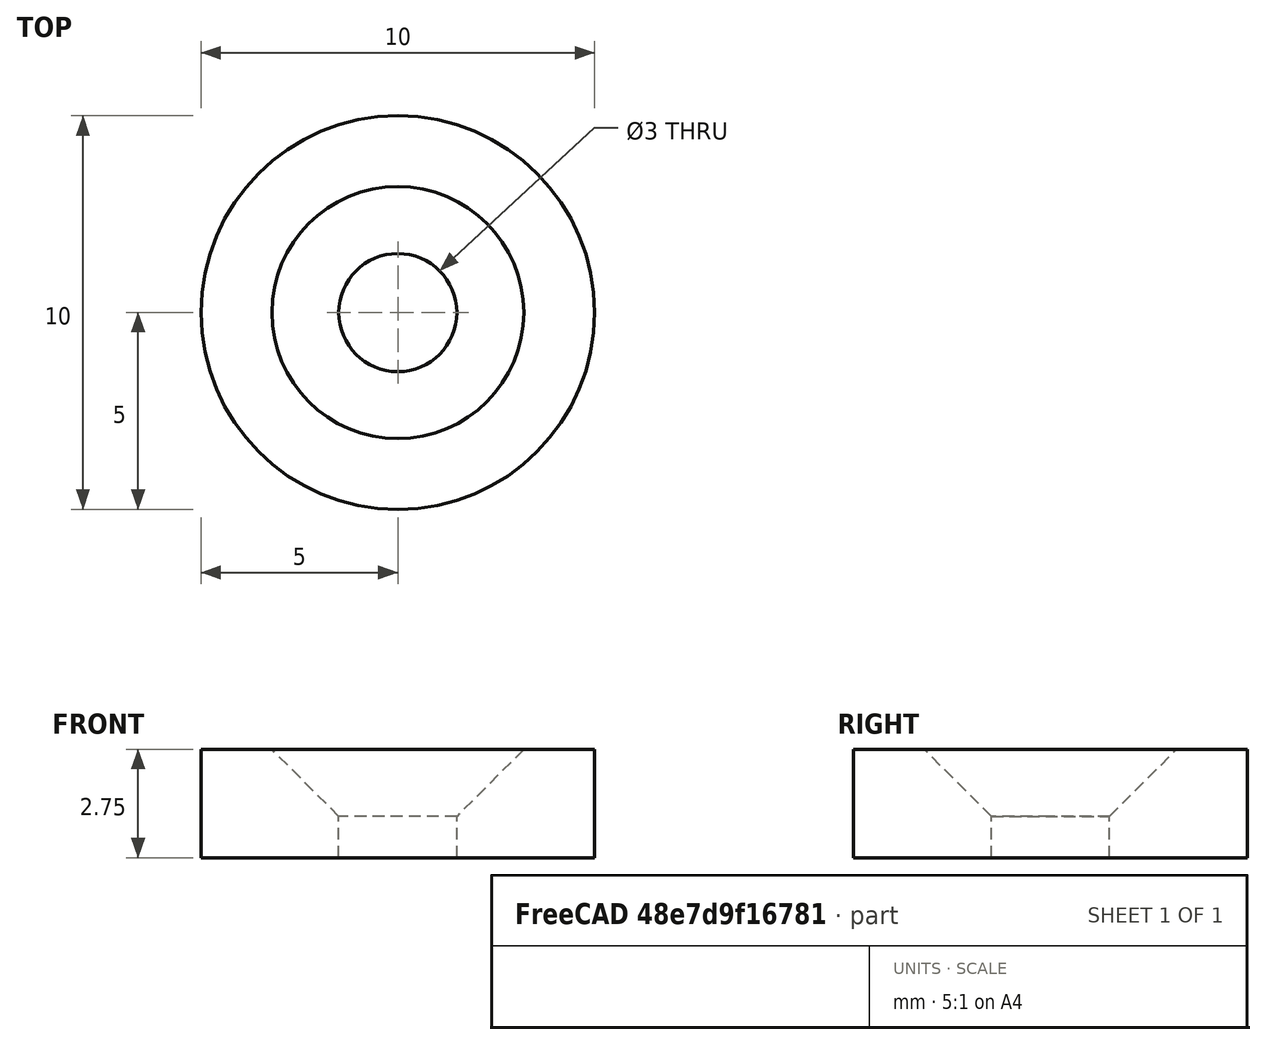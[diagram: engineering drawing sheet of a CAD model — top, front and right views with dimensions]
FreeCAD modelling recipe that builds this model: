
FCSTD DOCUMENT  (FreeCAD 0.19R23323 (Git))
Label: RingMagnet10x2.75
License: All rights reserved
LicenseURL: http://en.wikipedia.org/wiki/All_rights_reserved
objects: Sketcher::SketchObject×1, PartDesign::Revolution×1, PartDesign::Body×1
note: 4 computed .brp shape members not serialized (recipe doc carries the construction recipe); baked Part::Feature solids carry a one-line shape summary decoded from their .brp

FEATURE [Sketcher::SketchObject] Sketch
  MapMode = 5
  Placement = pos=(0,0,0) rot=(1,0,0;1.5708rad)
  Support = -> [XZ_Plane]
  sketch-geometry (5):
    g0: LineSegment StartX=3.2 StartY=2.75 StartZ=0 EndX=5 EndY=2.75 EndZ=0
    g1: LineSegment StartX=5 StartY=2.75 StartZ=0 EndX=5 EndY=0 EndZ=0
    g2: LineSegment StartX=5 StartY=0 StartZ=0 EndX=1.5 EndY=0 EndZ=0
    g3: LineSegment StartX=1.5 StartY=0 StartZ=0 EndX=1.5 EndY=1.05 EndZ=0
    g4: LineSegment StartX=3.2 StartY=2.75 StartZ=0 EndX=1.5 EndY=1.05 EndZ=0
  constraints (15):
    c: Coincident(g0,g1)
    c: Coincident(g1,g2)
    c: Coincident(g2,g3)
    c: Horizontal(g0)
    c: Horizontal(g2)
    c: Vertical(g1)
    c: Vertical(g3)
    c: PointOnObject(g1,g-1)
    c: DistanceX(g1) = 5
    c: Coincident(g0,g4)
    c: Coincident(g4,g3)
    c: DistanceY(g0) = 2.75
    c: DistanceX(g2) = 1.5
    c: Angle(g3,g4) = 2.35619
    c: DistanceX(g0) = 3.2
FEATURE [PartDesign::Revolution] Revolution
  Angle = 360
  Axis = (-3e-16,3e-16,1)
  Base = (0,0,0)
  Placement = pos=(0,0,0) rot=(1,0,0;1.5708rad)
  Profile = -> Sketch
  ReferenceAxis = -> Z_Axis
  Reversed = true
FEATURE [PartDesign::Body] Body  label="RingMagnet10x2.75"
  Group = -> [Sketch,Revolution]
  Origin = -> Origin
  Tip = -> Revolution
